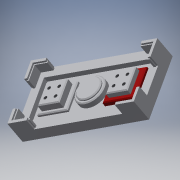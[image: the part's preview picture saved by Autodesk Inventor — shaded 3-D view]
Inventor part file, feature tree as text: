
AUTODESK INVENTOR PART (.ipt)
format: ipt  version: 2019 (Build 230136000, 136)  size: 377,344 bytes
history: native  units: mm
features: sketch x12, extrude x10, chamfer x5, hole x2
ambient origin geometry x8: Origin, YZ Plane, XZ Plane, XY Plane, X Axis, Y Axis, Z Axis, Center Point
bodies: Solid1 (feature_tree)
feature tree (29):
  extrude  "Extrusion1"  Depth=124.5mm
  extrude  "Extrusion2"  TaperAngle=0.0deg  [1 undecoded]
  extrude  "Extrusion3"  Depth=15.4mm
  extrude  "Extrusion4"  Depth=2.9mm
  extrude  "Extrusion5"  Depth=2.9mm
  extrude  "Extrusion6"  Depth=15.4mm
  extrude  "Extrusion7"  Depth=2.9mm
  extrude  "Extrusion8"  TaperAngle=0.0deg  [1 undecoded]
  extrude  "Extrusion10"  Depth=9.0mm
  extrude  "Extrusion11"  Depth=10.0mm
  chamfer  "Chamfer1"  [1 undecoded]
  chamfer  "Chamfer2"  Distance=32.5mm
  chamfer  "Chamfer3"  Distance=31.5mm
  chamfer  "Chamfer4"  Distance=16.65mm
  hole  "Hole1"  [1 undecoded]
  hole  "Hole2"  [1 undecoded]
  chamfer  "Chamfer5"  [1 undecoded]
  sketch  "Sketch1"  dims[d0=64.8mm d2=124.5mm]
  sketch  "Sketch2"  dims[d3=11.45mm d4=0.0mm]
  sketch  "Sketch3"  dims[d5=18.85mm d7=15.4mm]
  sketch  "Sketch4"  dims[d8=2.9mm d9=2.9mm]
  sketch  "Sketch5"  dims[d10=18.85mm d11=2.9mm]
  sketch  "Sketch6"  dims[d12=2.9mm d13=15.4mm]
  sketch  "Sketch7"  dims[d21=15.4mm d22=18.85mm d23=2.9mm d24=2.9mm]
  sketch  "Sketch8"  dims[d28=15.4mm d29=2.9mm d30=2.9mm d31=18.85mm d32=15.4mm d33=2.9mm d34=18.85mm d36=2.9mm]
  sketch  "Sketch10"  dims[d39=11.3mm d40=0.0mm]
  sketch  "Sketch11"  dims[d41=9.0mm d42=9.0mm]
  sketch  "Sketch12"  dims[d43=10.0mm d44=10.0mm]
  sketch  "Sketch14"  dims[d45=5.1mm d46=0.0mm d47=32.5mm d49=31.5mm d50=16.65mm d51=3.6mm d52=4.6mm d53=0.0mm d54=21.4mm d56=23.9mm d57=5.5mm d58=0.0mm d59=29.6mm d61=30.0mm d62=4.52mm d63=2.8mm d64=0.0mm d65=21.4mm d67=23.9mm d68=7.3mm d69=0.0mm d70=1.0mm d72=1.0mm d73=1.0mm d74=1.0mm d76=2.2mm d77=2.2mm d78=1.0mm d79=1.0mm d80=1.0mm d81=1.0mm d82=2.2mm d83=2.2mm d86=2.2mm d87=1.0mm d88=1.0mm d89=1.0mm d90=1.0mm d91=2.2mm d92=2.2mm d93=1.0mm d94=1.0mm d95=1.0mm d96=1.0mm d97=2.2mm d98=2.2mm d99=1.0mm d100=1.0mm d101=1.0mm d102=1.0mm d103=2.2mm d106=9.5mm d107=0.0mm d133=29.0mm d135=6.0mm d136=0.0mm d137=24.0mm d139=2.0mm d140=0.0mm d141=1.0mm d142=2.0mm d143=45.0deg d144=1.0mm d145=2.0mm d146=45.0deg d147=1.0mm d148=2.0mm d149=45.0deg d150=1.0mm d151=2.0mm d152=45.0deg d153=10.0mm d155=10.0mm d157=5.0mm d159=5.7mm d160=3.459mm d161=6.0mm d162=4.0mm d163=2.0mm d164=90.0deg d165=7.0mm d166=20.594885mm d167=10.0mm d169=10.0mm d170=5.0mm d171=5.7mm d172=3.459mm d173=6.0mm d174=4.0mm d175=2.0mm d176=90.0deg d177=7.0mm d178=20.594885mm d179=1.0mm d180=2.0mm d181=45.0deg]
note: 6 required parameter values undecoded (feature->parameter linkage not recoverable at this tier; creation-order binding heuristic only, values carry confidence <= 0.55)
